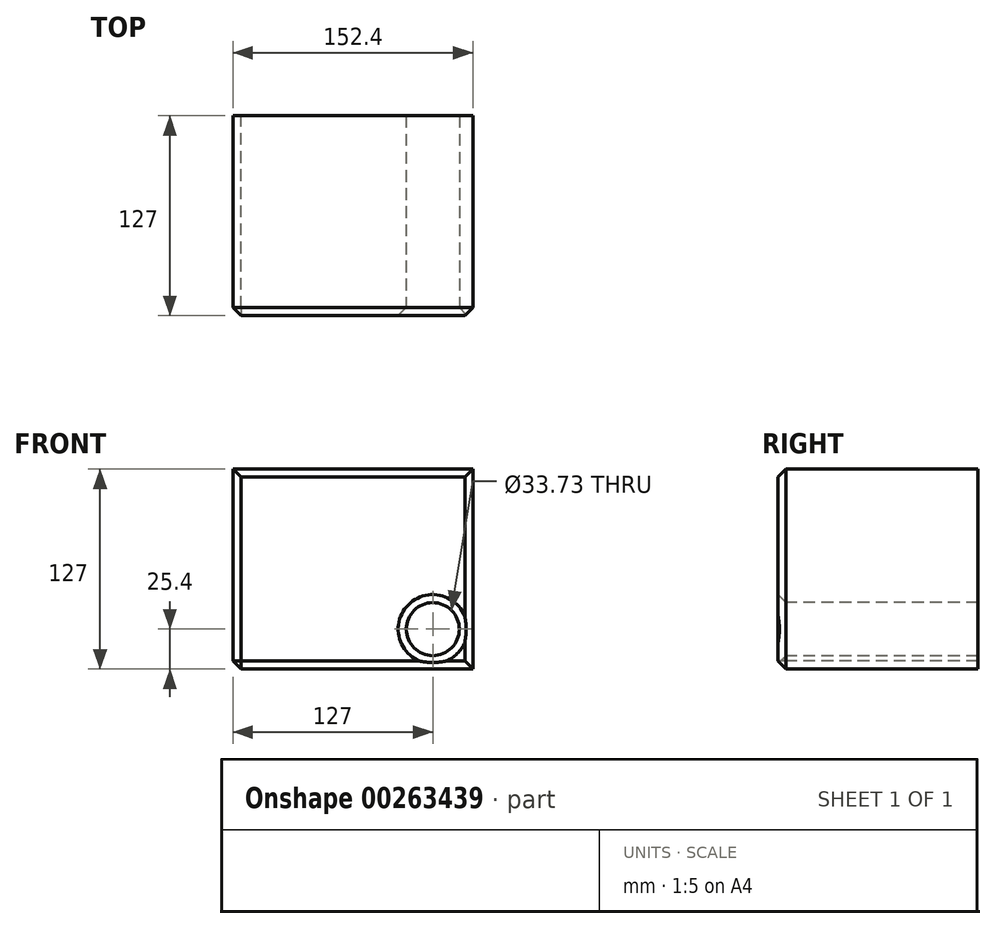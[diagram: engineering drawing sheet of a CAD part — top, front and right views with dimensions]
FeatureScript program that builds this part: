
annotation { "Feature Type Name" : "Feature", "Feature Type Description" : "" }
export const myFeature = defineFeature(function(context is Context, id is Id, definition is map)
    precondition{}
    {
        {
            var Q0;
            Q0=qCreatedBy(makeId("Front.planeOp"),FACE);
            var sketch = newSketch(context, id + "F0", { "sketchPlane" : qUnion([Q0])});
            skLineSegment(sketch, "E0.bottom", {"start": v(0, 0) * mm, "end": v(152.4, 0) * mm});
            skLineSegment(sketch, "E0.top", {"start": v(0, 127) * mm, "end": v(152.4, 127) * mm});
            skLineSegment(sketch, "E0.left", {"start": v(0, 0) * mm, "end": v(0, 127) * mm});
            skLineSegment(sketch, "E0.right", {"start": v(152.4, 0) * mm, "end": v(152.4, 127) * mm});
            skSolve(sketch);
        }
        {
            var Q0;
            Q0=makeQuery(id+"F0.imprint","IMPRINT",FACE,{"disambiguationData":[TD([[makeQuery(id+"F0.imprint","IMPRINT",EDGE,{"derivedFrom":sQuery(id+"F0.wireOp",EDGE,"E0.bottom")}),1.0]])]});
            var Q1;
            Q1=sQuery(id+"F0.wireOp",EDGE,"E0.top");
            var Q2;
            Q2=sQuery(id+"F0.wireOp",EDGE,"E0.left");
            var Q3;
            Q3=sQuery(id+"F0.wireOp",EDGE,"E0.right");
            var Q4;
            Q4=sQuery(id+"F0.wireOp",EDGE,"E0.bottom");
            extrude(context, id + "F1", {"entities" : qUnion([Q0]), "surfaceEntities" : qUnion([Q1, Q2, Q3, Q4]), "depth" : 127 * mm});
        }
        {
            var Q0;
            Q0=makeQuery(id+"F1.opExtrude","CAP_FACE",FACE,{"disambiguationData":[OSD([sQuery(id+"F0.wireOp",EDGE,"E0.bottom"),sQuery(id+"F0.wireOp",EDGE,"E0.top"),sQuery(id+"F0.wireOp",EDGE,"E0.left"),sQuery(id+"F0.wireOp",EDGE,"E0.right")])],"isStart":false});
            var sketch = newSketch(context, id + "F2", { "sketchPlane" : qUnion([Q0])});
            skLineSegment(sketch, "E1.bottom", {"start": v(152.4, 0) * mm, "end": v(101.6, 0) * mm});
            skLineSegment(sketch, "E1.top", {"start": v(152.4, 50.8) * mm, "end": v(101.6, 50.8) * mm});
            skLineSegment(sketch, "E1.left", {"start": v(152.4, 0) * mm, "end": v(152.4, 50.8) * mm});
            skLineSegment(sketch, "E1.right", {"start": v(101.6, 0) * mm, "end": v(101.6, 50.8) * mm});
            skSolve(sketch);
        }
        {
            var Q0;
            Q0=makeQuery(id+"F2.imprint","IMPRINT",FACE,{"disambiguationData":[TD([[makeQuery(id+"F2.imprint","IMPRINT",EDGE,{"derivedFrom":sQuery(id+"F2.wireOp",EDGE,"E1.bottom")}),1.0]])]});
            var sketch = newSketch(context, id + "F3", { "sketchPlane" : qUnion([Q0])});
            skCircle(sketch, "E2", {"center": v(127, 25.4) * mm, "radius": 16.87 * mm});
            skSolve(sketch);
        }
        {
            var Q0;
            Q0=makeQuery(id+"F3.imprint","IMPRINT",FACE,{"disambiguationData":[TD([[makeQuery(id+"F3.imprint","IMPRINT",EDGE,{"derivedFrom":sQuery(id+"F3.wireOp",EDGE,"E2")}),1.0]])]});
            extrude(context, id + "F4", {"entities" : qUnion([Q0]), "operationType" : NewBodyOperationType.REMOVE, "endBound" : BoundingType.THROUGH_ALL, "oppositeDirection" : true, "depth" : 25.4 * mm});
        }
        {
            var Q0;
            Q0=makeQuery(id+"F1.opExtrude","SWEPT_EDGE",EDGE,{"disambiguationData":[OSD([sQuery(id+"F0.wireOp",EDGE,"E0.bottom"),sQuery(id+"F0.wireOp",EDGE,"E0.left")])]});
            var Q1;
            Q1=makeQuery(id+"F1.opExtrude","CAP_FACE",FACE,{"disambiguationData":[OSD([sQuery(id+"F0.wireOp",EDGE,"E0.bottom"),sQuery(id+"F0.wireOp",EDGE,"E0.top"),sQuery(id+"F0.wireOp",EDGE,"E0.left"),sQuery(id+"F0.wireOp",EDGE,"E0.right")])],"isStart":false});
            chamfer(context, id + "F5", {"entities" : qUnion([Q0, Q1]), "width" : 5.08 * mm, "tangentPropagation" : true});
        }
    });
